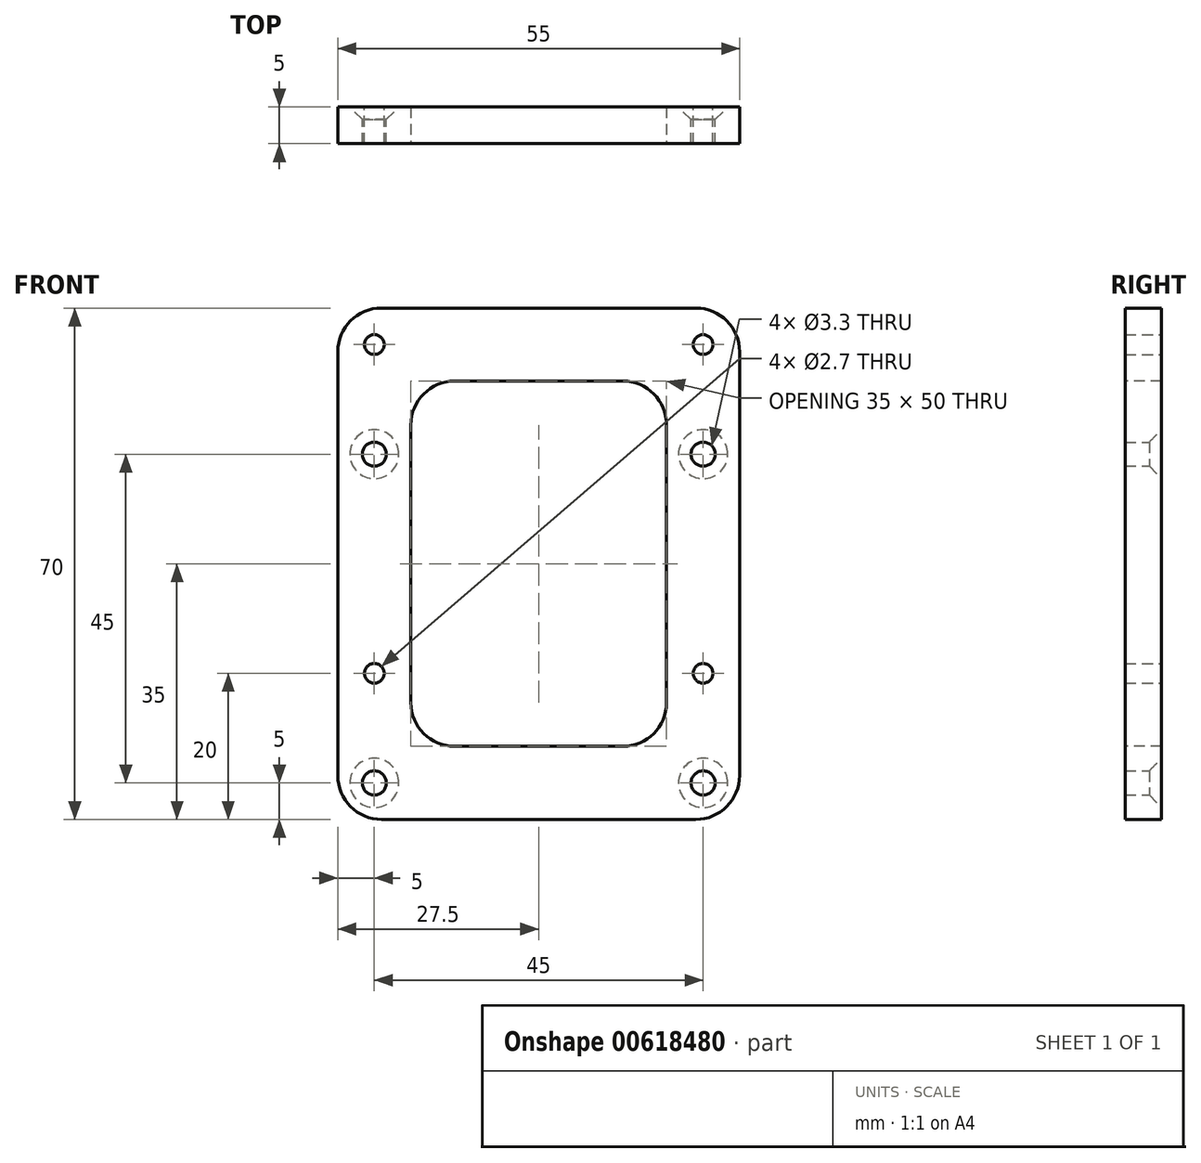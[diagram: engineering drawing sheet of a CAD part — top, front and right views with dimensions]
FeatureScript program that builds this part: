
annotation { "Feature Type Name" : "Feature", "Feature Type Description" : "" }
export const myFeature = defineFeature(function(context is Context, id is Id, definition is map)
    precondition{}
    {
        {
            var Q0;
            Q0=qCreatedBy(makeId("Front.planeOp"),FACE);
            var sketch = newSketch(context, id + "F0", { "sketchPlane" : qUnion([Q0])});
            skLineSegment(sketch, "E0.bottom", {"start": v(22.5, 30) * mm, "end": v(-22.5, 30) * mm, "construction": true});
            skLineSegment(sketch, "E0.top", {"start": v(22.5, -30) * mm, "end": v(-22.5, -30) * mm, "construction": true});
            skLineSegment(sketch, "E0.left", {"start": v(22.5, 30) * mm, "end": v(22.5, -30) * mm, "construction": true});
            skLineSegment(sketch, "E0.right", {"start": v(-22.5, 30) * mm, "end": v(-22.5, -30) * mm, "construction": true});
            skPoint(sketch, "E0.middle", {"position": v(0, 0) * mm});
            skLineSegment(sketch, "E1.0", {"start": v(27.5, 35) * mm, "end": v(-27.5, 35) * mm});
            skLineSegment(sketch, "E1.1", {"start": v(27.5, 35) * mm, "end": v(27.5, -35) * mm});
            skLineSegment(sketch, "E1.2", {"start": v(27.5, -35) * mm, "end": v(-27.5, -35) * mm});
            skLineSegment(sketch, "E1.3", {"start": v(-27.5, 35) * mm, "end": v(-27.5, -35) * mm});
            skLineSegment(sketch, "E2", {"start": v(-22.5, -15) * mm, "end": v(22.5, -15) * mm, "construction": true});
            skLineSegment(sketch, "E3", {"start": v(-22.5, 15) * mm, "end": v(22.5, 15) * mm, "construction": true});
            skSolve(sketch);
        }
        {
            var Q0;
            Q0=makeQuery(id+"F0.imprint","IMPRINT",FACE,{"disambiguationData":[TD([[makeQuery(id+"F0.imprint","IMPRINT",EDGE,{"derivedFrom":sQuery(id+"F0.wireOp",EDGE,"E1.0")}),1.0]])]});
            extrude(context, id + "F1", {"entities" : qUnion([Q0]), "depth" : 5 * mm, "offsetDistance" : 25 * mm});
        }
        {
            var Q0;
            Q0=sQuery(id+"F0.wireOp",VERTEX,"E3.end");
            var Q1;
            Q1=sQuery(id+"F0.wireOp",VERTEX,"E0.left.end");
            var Q2;
            Q2=sQuery(id+"F0.wireOp",VERTEX,"E0.right.end");
            var Q3;
            Q3=sQuery(id+"F0.wireOp",VERTEX,"E3.start");
            var Q4;
            Q4=makeQuery(id+"F1.opExtrude","SWEPT_BODY",BODY,{"disambiguationData":[OSD([sQuery(id+"F0.wireOp",EDGE,"E1.0"),sQuery(id+"F0.wireOp",EDGE,"E1.1"),sQuery(id+"F0.wireOp",EDGE,"E1.2"),sQuery(id+"F0.wireOp",EDGE,"E1.3")])]});
            hole(context, id + "F2", {"style" : HoleStyle.C_SINK, "endStyle" : HoleEndStyle.THROUGH, "oppositeDirection" : true, "standardTappedOrClearance" : lookupTablePath({ "standard" : "ISO", "fit" : "Normal", "size" : "M3", "type" : "Clearance" }), "standardBlindInLast" : lookupTablePath({ "fit" : "Standard", "standard" : "ISO", "size" : "M3", "type" : "Clearance" }), "holeDiameter" : 3.3 * mm, "cSinkDiameter" : 6.72 * mm, "cSinkAngle" : 90 * degree, "majorDiameter" : 5 * mm, "isTappedThrough" : true, "tappedDepth" : 12 * mm, "tapClearance" : 3, "startFromSketch" : true, "locations" : qUnion([Q0, Q1, Q2, Q3]), "scope" : qUnion([Q4])});
        }
        {
            var Q0;
            Q0=sQuery(id+"F0.wireOp",VERTEX,"E0.bottom.start");
            var Q1;
            Q1=sQuery(id+"F0.wireOp",VERTEX,"E0.right.start");
            var Q2;
            Q2=sQuery(id+"F0.wireOp",VERTEX,"E2.start");
            var Q3;
            Q3=sQuery(id+"F0.wireOp",VERTEX,"E2.end");
            var Q4;
            Q4=makeQuery(id+"F1.opExtrude","SWEPT_BODY",BODY,{"disambiguationData":[OSD([sQuery(id+"F0.wireOp",EDGE,"E1.0"),sQuery(id+"F0.wireOp",EDGE,"E1.1"),sQuery(id+"F0.wireOp",EDGE,"E1.2"),sQuery(id+"F0.wireOp",EDGE,"E1.3")])]});
            hole(context, id + "F3", {"style" : HoleStyle.SIMPLE, "endStyle" : HoleEndStyle.THROUGH, "oppositeDirection" : true, "standardTappedOrClearance" : lookupTablePath({ "standard" : "ISO", "engagement" : "50%", "pitch" : "0.5 mm", "size" : "M3", "type" : "Tapped" }), "standardBlindInLast" : lookupTablePath({ "standard" : "ISO", "engagement" : "50%", "pitch" : "0.5 mm", "size" : "M3", "type" : "Tapped" }), "holeDiameter" : 2.7 * mm, "majorDiameter" : 3 * mm, "showTappedDepth" : true, "isTappedThrough" : true, "tappedDepth" : 12 * mm, "tapClearance" : 3, "startFromSketch" : true, "locations" : qUnion([Q0, Q1, Q2, Q3]), "scope" : qUnion([Q4])});
        }
        {
            var Q0;
            Q0=makeQuery(id+"F1.opExtrude","CAP_FACE",FACE,{"disambiguationData":[OSD([sQuery(id+"F0.wireOp",EDGE,"E1.0"),sQuery(id+"F0.wireOp",EDGE,"E1.1"),sQuery(id+"F0.wireOp",EDGE,"E1.2"),sQuery(id+"F0.wireOp",EDGE,"E1.3")])],"isStart":false});
            var sketch = newSketch(context, id + "F4", { "sketchPlane" : qUnion([Q0])});
            skLineSegment(sketch, "E4.0", {"start": v(17.5, 25) * mm, "end": v(-17.5, 25) * mm});
            skLineSegment(sketch, "E4.1", {"start": v(17.5, -25) * mm, "end": v(17.5, 25) * mm});
            skLineSegment(sketch, "E4.2", {"start": v(-17.5, -25) * mm, "end": v(17.5, -25) * mm});
            skLineSegment(sketch, "E4.3", {"start": v(-17.5, 25) * mm, "end": v(-17.5, -25) * mm});
            skSolve(sketch);
        }
        {
            var Q0;
            Q0=makeQuery(id+"F4.imprint","IMPRINT",FACE,{"disambiguationData":[TD([[makeQuery(id+"F4.imprint","IMPRINT",EDGE,{"derivedFrom":sQuery(id+"F4.wireOp",EDGE,"E4.0")}),1.0]])]});
            extrude(context, id + "F5", {"entities" : qUnion([Q0]), "operationType" : NewBodyOperationType.REMOVE, "endBound" : BoundingType.UP_TO_NEXT, "oppositeDirection" : true, "depth" : 25 * mm, "offsetDistance" : 25 * mm});
        }
        {
            var Q0;
            Q0=makeQuery(id+"F1.opExtrude","SWEPT_EDGE",EDGE,{"disambiguationData":[OSD([sQuery(id+"F0.wireOp",EDGE,"E1.0"),sQuery(id+"F0.wireOp",EDGE,"E1.3")])]});
            var Q1;
            Q1=makeQuery(id+"F1.opExtrude","SWEPT_EDGE",EDGE,{"disambiguationData":[OSD([sQuery(id+"F0.wireOp",EDGE,"E1.2"),sQuery(id+"F0.wireOp",EDGE,"E1.3")])]});
            var Q2;
            Q2=makeQuery(id+"F1.opExtrude","SWEPT_EDGE",EDGE,{"disambiguationData":[OSD([sQuery(id+"F0.wireOp",EDGE,"E1.0"),sQuery(id+"F0.wireOp",EDGE,"E1.1")])]});
            var Q3;
            Q3=makeQuery(id+"F1.opExtrude","SWEPT_EDGE",EDGE,{"disambiguationData":[OSD([sQuery(id+"F0.wireOp",EDGE,"E1.1"),sQuery(id+"F0.wireOp",EDGE,"E1.2")])]});
            var Q4;
            Q4=makeQuery(id+"F5.boolean.opBoolean","COPY",EDGE,{"derivedFrom":makeQuery(id+"F5.opExtrude","SWEPT_EDGE",EDGE,{"disambiguationData":[OSD([sQuery(id+"F4.wireOp",EDGE,"E4.2"),sQuery(id+"F4.wireOp",EDGE,"E4.3")])]})});
            var Q5;
            Q5=makeQuery(id+"F5.boolean.opBoolean","COPY",EDGE,{"derivedFrom":makeQuery(id+"F5.opExtrude","SWEPT_EDGE",EDGE,{"disambiguationData":[OSD([sQuery(id+"F4.wireOp",EDGE,"E4.0"),sQuery(id+"F4.wireOp",EDGE,"E4.1")])]})});
            var Q6;
            Q6=makeQuery(id+"F5.boolean.opBoolean","COPY",EDGE,{"derivedFrom":makeQuery(id+"F5.opExtrude","SWEPT_EDGE",EDGE,{"disambiguationData":[OSD([sQuery(id+"F4.wireOp",EDGE,"E4.1"),sQuery(id+"F4.wireOp",EDGE,"E4.2")])]})});
            var Q7;
            Q7=makeQuery(id+"F5.boolean.opBoolean","COPY",EDGE,{"derivedFrom":makeQuery(id+"F5.opExtrude","SWEPT_EDGE",EDGE,{"disambiguationData":[OSD([sQuery(id+"F4.wireOp",EDGE,"E4.0"),sQuery(id+"F4.wireOp",EDGE,"E4.3")])]})});
            fillet(context, id + "F6", {"entities" : qUnion([Q0, Q1, Q2, Q3, Q4, Q5, Q6, Q7]), "radius" : 6 * mm, "tangentPropagation" : true, "allowEdgeOverflow" : false});
        }
    });
